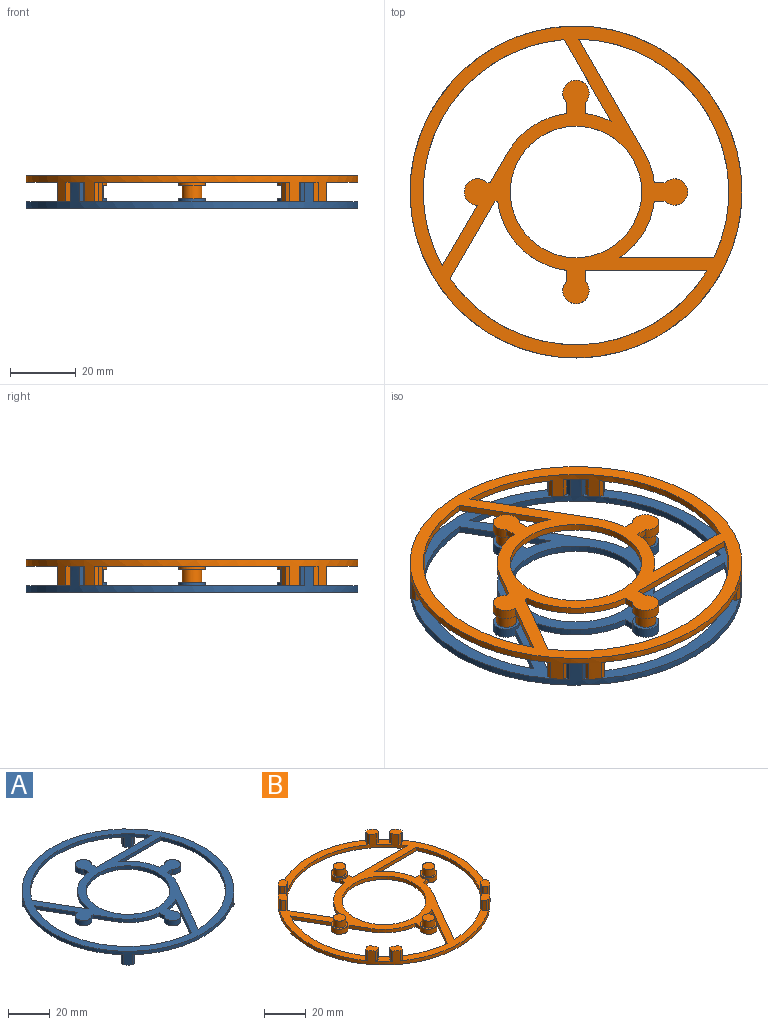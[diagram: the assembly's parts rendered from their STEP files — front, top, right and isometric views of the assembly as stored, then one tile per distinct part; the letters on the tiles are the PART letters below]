
ASSEMBLY  parts=2 mates=1
PART A: 64 faces, bbox 101x101x8 mm
  f0: plane 101x84.83mm, normal (0,0,-1), area 1819mm2, adj f2,f3,f4,f5,f6,f7,f8,f9
  f1: plane 68.66x16.42mm, normal (0,0,-1), area 284.2mm2, adj f3,f22,f37,f46,f48,f49,f50,f53
  f2: plane 23.61x13.63mm, normal (0.87,0.5,0), area 54.5mm2, adj f0,f3,f23,f27
  f3: cylinder r=46.5mm len=78.14mm, axis (0,0,1), area 227.1mm2, adj f0,f1,f2,f4,f27,f38,f47,f48
  f4: plane 37.08x2mm, normal (0,1,0), area 74.2mm2, adj f0,f3,f5,f27
  f5: plane 3.1x2mm, normal (1,0,0), area 6.2mm2, adj f0,f4,f27,f32
  f6: plane 3.25x2mm, normal (-1,0,0), area 6.5mm2, adj f0,f7,f27,f32
  f7: cylinder r=24mm len=21.09mm, axis (0,0,1), area 64.4mm2, adj f0,f6,f23,f27
  f8: cylinder r=46.5mm len=68.85mm, axis (0,0,1), area 206.4mm2, adj f0,f9,f24,f27,f41,f60,f62
  f9: plane 18.49x10.68mm, normal (-0.87,-0.5,0), area 42.7mm2, adj f0,f8,f27,f30
  f10: plane 2x0.97mm, normal (0,-1,0), area 1.9mm2, adj f0,f11,f27,f30
  f11: plane 9.25x5.34mm, normal (-0.87,-0.5,0), area 21.4mm2, adj f0,f10,f12,f27
  f12: cylinder r=24mm len=18.03mm, axis (0,0,1), area 44.8mm2, adj f0,f11,f13,f27
  f13: plane 3.25x2mm, normal (-1,0,0), area 6.5mm2, adj f0,f12,f27,f28
  f14: plane 3.25x2mm, normal (1,0,0), area 6.5mm2, adj f0,f15,f27,f28
  f15: cylinder r=24mm len=7.94mm, axis (0,0,1), area 16.6mm2, adj f0,f14,f24,f27
  f16: cylinder r=46.5mm len=66.49mm, axis (0,0,1), area 206.4mm2, adj f0,f17,f25,f27,f44,f58,f59
  f17: plane 34.49x19.91mm, normal (0.87,-0.5,0), area 79.7mm2, adj f0,f16,f18,f27
  f18: cylinder r=24mm len=9.25mm, axis (0,0,1), area 19.6mm2, adj f0,f17,f19,f27
  f19: plane 3.25x2mm, normal (0,-1,0), area 6.5mm2, adj f0,f18,f27,f34
  f20: plane 3.25x2mm, normal (0,1,0), area 6.5mm2, adj f0,f21,f27,f34
  f21: cylinder r=24mm len=17.25mm, axis (0,0,1), area 41.8mm2, adj f0,f20,f25,f27
  f22: cylinder r=50.5mm len=101mm, axis (0,0,1), area 726.7mm2, adj f0,f1,f27,f38,f41,f44,f47,f49
  f23: plane 2x0.84mm, normal (0,1,0), area 1.7mm2, adj f0,f2,f7,f27
  f24: plane 24.87x14.36mm, normal (-0.87,0.5,0), area 57.4mm2, adj f0,f8,f15,f27
  f25: plane 28.71x2mm, normal (0,-1,0), area 57.4mm2, adj f0,f16,f21,f27
  f26: cylinder r=20mm len=40mm, axis (0,0,1), area 251.3mm2, adj f0,f27
  f27: plane 101x101mm, normal (0,0,1), area 2386.5mm2, adj f2,f3,f4,f5,f6,f7,f8,f9
  f28: cylinder r=4mm len=8mm, axis (0,0,1), area 63.3mm2, adj f0,f13,f14,f27,f29
  f29: plane 8x8mm, normal (0,0,-1), area 50.3mm2, adj f28
  f30: cylinder r=4mm len=8mm, axis (0,0,1), area 56.7mm2, adj f0,f9,f10,f27,f31
  f31: plane 8x8mm, normal (0,0,-1), area 50.3mm2, adj f30
  f32: cylinder r=4mm len=8mm, axis (0,0,1), area 63.3mm2, adj f0,f5,f6,f27,f33
  f33: plane 8x8mm, normal (0,0,-1), area 50.3mm2, adj f32
  f34: cylinder r=4mm len=8mm, axis (0,0,1), area 63.3mm2, adj f0,f19,f20,f27,f35
  f35: plane 8x8mm, normal (0,0,-1), area 50.3mm2, adj f34
  f36: plane 6x1.49mm, normal (-0.66,-0.75,0), area 12mm2, adj f0,f38,f51,f52
  f37: plane 6x1.49mm, normal (0.75,0.66,0), area 12mm2, adj f1,f38,f50,f53
  f38: plane 5.47x5.47mm, normal (0,0,-1), area 20.6mm2, adj f3,f22,f36,f37,f50,f51,f52,f53
  f39: plane 6x1.49mm, normal (-0.66,0.75,0), area 12mm2, adj f0,f41,f60,f61
  f40: plane 6x1.49mm, normal (0.75,-0.66,0), area 12mm2, adj f0,f41,f62,f63
  f41: plane 5.47x5.47mm, normal (0,0,-1), area 20.6mm2, adj f8,f22,f39,f40,f60,f61,f62,f63
  f42: plane 6x1.49mm, normal (-0.75,-0.66,0), area 12mm2, adj f0,f44,f56,f58
  f43: plane 6x1.49mm, normal (0.66,0.75,0), area 12mm2, adj f0,f44,f57,f59
  f44: plane 5.47x5.47mm, normal (0,0,-1), area 20.6mm2, adj f16,f22,f42,f43,f56,f57,f58,f59
  f45: plane 6x1.49mm, normal (0.66,-0.75,0), area 12mm2, adj f0,f47,f54,f55
  f46: plane 6x1.49mm, normal (-0.75,0.66,0), area 12mm2, adj f1,f47,f48,f49
  f47: plane 5.47x5.47mm, normal (0,0,-1), area 20.6mm2, adj f3,f22,f45,f46,f48,f49,f54,f55
  f48: plane 6x1.4mm, normal (-1,-0.05,0), area 8.4mm2, adj f1,f3,f46,f47
  f49: plane 6x1.43mm, normal (-0.05,1,0), area 8.6mm2, adj f1,f22,f46,f47
  f50: plane 6x1.43mm, normal (0.05,1,0), area 8.6mm2, adj f1,f22,f37,f38
  f51: plane 6x1.43mm, normal (-1,-0.05,0), area 8.6mm2, adj f0,f22,f36,f38
  f52: plane 6x1.4mm, normal (0.05,-1,0), area 8.4mm2, adj f0,f3,f36,f38
  f53: plane 6x1.4mm, normal (1,-0.05,0), area 8.4mm2, adj f1,f3,f37,f38
  f54: plane 6x1.43mm, normal (1,-0.05,0), area 8.6mm2, adj f0,f22,f45,f47
  f55: plane 6x1.4mm, normal (-0.05,-1,0), area 8.4mm2, adj f0,f3,f45,f47
  f56: plane 6x1.43mm, normal (-0.05,-1,0), area 8.6mm2, adj f0,f22,f42,f44
  f57: plane 6x1.43mm, normal (1,0.05,0), area 8.6mm2, adj f0,f22,f43,f44
  f58: plane 6x1.4mm, normal (-1,0.05,0), area 8.4mm2, adj f0,f16,f42,f44
  f59: plane 6x1.4mm, normal (-0.05,1,0), area 8.4mm2, adj f0,f16,f43,f44
  f60: plane 6x1.4mm, normal (0.05,1,0), area 8.4mm2, adj f0,f8,f39,f41
  f61: plane 6x1.43mm, normal (-1,0.05,0), area 8.6mm2, adj f0,f22,f39,f41
  f62: plane 6x1.4mm, normal (1,0.05,0), area 8.4mm2, adj f0,f8,f40,f41
  f63: plane 6x1.43mm, normal (0.05,-1,0), area 8.6mm2, adj f0,f22,f40,f41
PART B: 104 faces, bbox 101x101x8 mm
  f0: plane 8.22x8.22mm, normal (0,0,1), area 24.6mm2, adj f7,f26,f67,f69,f75,f79,f80,f81
  f1: plane 101x80.3mm, normal (0,0,1), area 1683.5mm2, adj f6,f7,f8,f9,f10,f11,f12,f13
  f2: plane 8.22x8.22mm, normal (0,0,1), area 24.6mm2, adj f20,f26,f61,f63,f96,f97,f98,f99
  f3: plane 8.22x8.22mm, normal (0,0,1), area 24.6mm2, adj f12,f26,f55,f57,f100,f101,f102,f103
  f4: plane 59.59x12.98mm, normal (0,0,1), area 239mm2, adj f7,f26,f52,f70,f74,f76,f82,f84
  f5: plane 8.22x8.22mm, normal (0,0,1), area 24.6mm2, adj f7,f26,f49,f51,f72,f83,f85,f86
  f6: plane 23.61x13.63mm, normal (0.87,0.5,0), area 54.5mm2, adj f1,f7,f27,f31
  f7: cylinder r=46.5mm len=78.14mm, axis (0,0,-1), area 268.6mm2, adj f0,f1,f4,f5,f6,f8,f31,f50
  f8: plane 37.08x2mm, normal (0,1,0), area 74.2mm2, adj f1,f7,f9,f31
  f9: plane 3.1x2mm, normal (1,0,0), area 6.2mm2, adj f1,f8,f31,f36
  f10: plane 3.25x2mm, normal (-1,0,0), area 6.5mm2, adj f1,f11,f31,f36
  f11: cylinder r=24mm len=21.09mm, axis (0,0,-1), area 64.4mm2, adj f1,f10,f27,f31
  f12: cylinder r=46.5mm len=68.85mm, axis (0,0,-1), area 227.1mm2, adj f1,f3,f13,f28,f31,f56,f59,f92
  f13: plane 18.49x10.68mm, normal (-0.87,-0.5,0), area 42.7mm2, adj f1,f12,f31,f34
  f14: plane 2x0.97mm, normal (0,-1,0), area 1.9mm2, adj f1,f15,f31,f34
  f15: plane 9.25x5.34mm, normal (-0.87,-0.5,0), area 21.4mm2, adj f1,f14,f16,f31
  f16: cylinder r=24mm len=18.03mm, axis (0,0,-1), area 44.8mm2, adj f1,f15,f17,f31
  f17: plane 3.25x2mm, normal (-1,0,0), area 6.5mm2, adj f1,f16,f31,f32
  f18: plane 3.25x2mm, normal (1,0,0), area 6.5mm2, adj f1,f19,f31,f32
  f19: cylinder r=24mm len=7.94mm, axis (0,0,-1), area 16.6mm2, adj f1,f18,f28,f31
  f20: cylinder r=46.5mm len=66.49mm, axis (0,0,-1), area 227.1mm2, adj f1,f2,f21,f29,f31,f62,f65,f89
  f21: plane 34.49x19.91mm, normal (0.87,-0.5,0), area 79.7mm2, adj f1,f20,f22,f31
  f22: cylinder r=24mm len=9.25mm, axis (0,0,-1), area 19.6mm2, adj f1,f21,f23,f31
  f23: plane 3.25x2mm, normal (0,-1,0), area 6.5mm2, adj f1,f22,f31,f38
  f24: plane 3.25x2mm, normal (0,1,0), area 6.5mm2, adj f1,f25,f31,f38
  f25: cylinder r=24mm len=17.25mm, axis (0,0,-1), area 41.8mm2, adj f1,f24,f29,f31
  f26: cylinder r=50.5mm len=101mm, axis (0,0,-1), area 818.7mm2, adj f0,f1,f2,f3,f4,f5,f31,f50
  f27: plane 2x0.84mm, normal (0,1,0), area 1.7mm2, adj f1,f6,f11,f31
  f28: plane 24.87x14.36mm, normal (-0.87,0.5,0), area 57.4mm2, adj f1,f12,f19,f31
  f29: plane 28.71x2mm, normal (0,-1,0), area 57.4mm2, adj f1,f20,f25,f31
  f30: cylinder r=20mm len=40mm, axis (0,0,-1), area 251.3mm2, adj f1,f31
  f31: plane 101x101mm, normal (0,0,-1), area 2386.5mm2, adj f6,f7,f8,f9,f10,f11,f12,f13
  f32: cylinder r=4mm len=8mm, axis (0,0,-1), area 63.3mm2, adj f1,f17,f18,f31,f33
  f33: plane 8x8mm, normal (0,0,1), area 22mm2, adj f32,f44
  f34: cylinder r=4mm len=8mm, axis (0,0,-1), area 56.7mm2, adj f1,f13,f14,f31,f35
  f35: plane 8x8mm, normal (0,0,1), area 22mm2, adj f34,f42
  f36: cylinder r=4mm len=8mm, axis (0,0,-1), area 63.3mm2, adj f1,f9,f10,f31,f37
  f37: plane 8x8mm, normal (0,0,1), area 22mm2, adj f36,f40
  f38: cylinder r=4mm len=8mm, axis (0,0,-1), area 63.3mm2, adj f1,f23,f24,f31,f39
  f39: plane 8x8mm, normal (0,0,1), area 22mm2, adj f38,f46
  f40: cylinder r=3mm len=6mm, axis (0,0,-1), area 75.4mm2, adj f37,f41
  f41: plane 6x6mm, normal (0,0,1), area 28.3mm2, adj f40
  f42: cylinder r=3mm len=6mm, axis (0,0,-1), area 75.4mm2, adj f35,f43
  f43: plane 6x6mm, normal (0,0,1), area 28.3mm2, adj f42
  f44: cylinder r=3mm len=6mm, axis (0,0,-1), area 75.4mm2, adj f33,f45
  f45: plane 6x6mm, normal (0,0,1), area 28.3mm2, adj f44
  f46: cylinder r=3mm len=6mm, axis (0,0,-1), area 75.4mm2, adj f39,f47
  f47: plane 6x6mm, normal (0,0,1), area 28.3mm2, adj f46
  f48: plane 6x1.64mm, normal (-0.57,-0.82,0), area 12mm2, adj f1,f50,f73,f87
  f49: plane 6x1.49mm, normal (0.66,0.75,0), area 12mm2, adj f5,f50,f83,f86
  f50: plane 5.66x5.39mm, normal (0,0,1), area 20.6mm2, adj f7,f26,f48,f49,f73,f83,f86,f87
  f51: plane 6x1.49mm, normal (-0.75,-0.66,0), area 12mm2, adj f5,f53,f72,f85
  f52: plane 6x1.64mm, normal (0.82,0.57,0), area 12mm2, adj f4,f53,f82,f84
  f53: plane 5.66x5.39mm, normal (0,0,1), area 20.6mm2, adj f7,f26,f51,f52,f72,f82,f84,f85
  f54: plane 6x1.64mm, normal (-0.57,0.82,0), area 12mm2, adj f1,f56,f92,f93
  f55: plane 6x1.49mm, normal (0.66,-0.75,0), area 12mm2, adj f3,f56,f102,f103
  f56: plane 5.66x5.39mm, normal (0,0,1), area 20.6mm2, adj f12,f26,f54,f55,f92,f93,f102,f103
  f57: plane 6x1.49mm, normal (-0.75,0.66,0), area 12mm2, adj f3,f59,f100,f101
  f58: plane 6x1.64mm, normal (0.82,-0.57,0), area 12mm2, adj f1,f59,f94,f95
  f59: plane 5.66x5.39mm, normal (0,0,1), area 20.6mm2, adj f12,f26,f57,f58,f94,f95,f100,f101
  f60: plane 6x1.64mm, normal (-0.82,-0.57,0), area 12mm2, adj f1,f62,f90,f91
  f61: plane 6x1.49mm, normal (0.75,0.66,0), area 12mm2, adj f2,f62,f97,f99
  f62: plane 5.66x5.39mm, normal (0,0,1), area 20.6mm2, adj f20,f26,f60,f61,f90,f91,f97,f99
  f63: plane 6x1.49mm, normal (-0.66,-0.75,0), area 12mm2, adj f2,f65,f96,f98
  f64: plane 6x1.64mm, normal (0.57,0.82,0), area 12mm2, adj f1,f65,f88,f89
  f65: plane 5.66x5.39mm, normal (0,0,1), area 20.6mm2, adj f20,f26,f63,f64,f88,f89,f96,f98
  f66: plane 6x1.64mm, normal (0.57,-0.82,0), area 12mm2, adj f1,f68,f77,f78
  f67: plane 6x1.49mm, normal (-0.66,0.75,0), area 12mm2, adj f0,f68,f75,f79
  f68: plane 5.66x5.39mm, normal (0,0,1), area 20.6mm2, adj f7,f26,f66,f67,f75,f77,f78,f79
  f69: plane 6x1.49mm, normal (0.75,-0.66,0), area 12mm2, adj f0,f71,f80,f81
  f70: plane 6x1.64mm, normal (-0.82,0.57,0), area 12mm2, adj f4,f71,f74,f76
  f71: plane 5.66x5.39mm, normal (0,0,1), area 20.6mm2, adj f7,f26,f69,f70,f74,f76,f80,f81
  f72: plane 6x1.43mm, normal (-1,0.07,0), area 8.6mm2, adj f5,f26,f51,f53
  f73: plane 6x1.41mm, normal (-0.99,-0.16,0), area 8.6mm2, adj f1,f26,f48,f50
  f74: plane 6x1.38mm, normal (-0.99,-0.16,0), area 8.4mm2, adj f4,f7,f70,f71
  f75: plane 6x1.4mm, normal (-1,0.07,0), area 8.4mm2, adj f0,f7,f67,f68
  f76: plane 6x1.41mm, normal (-0.16,0.99,0), area 8.6mm2, adj f4,f26,f70,f71
  f77: plane 6x1.38mm, normal (-0.16,-0.99,0), area 8.4mm2, adj f1,f7,f66,f68
  f78: plane 6x1.41mm, normal (0.99,-0.16,0), area 8.6mm2, adj f1,f26,f66,f68
  f79: plane 6x1.43mm, normal (0.07,1,0), area 8.6mm2, adj f0,f26,f67,f68
  f80: plane 6x1.4mm, normal (0.07,-1,0), area 8.4mm2, adj f0,f7,f69,f71
  f81: plane 6x1.43mm, normal (1,0.07,0), area 8.6mm2, adj f0,f26,f69,f71
  f82: plane 6x1.41mm, normal (0.16,0.99,0), area 8.6mm2, adj f4,f26,f52,f53
  f83: plane 6x1.43mm, normal (-0.07,1,0), area 8.6mm2, adj f5,f26,f49,f50
  f84: plane 6x1.38mm, normal (0.99,-0.16,0), area 8.4mm2, adj f4,f7,f52,f53
  f85: plane 6x1.4mm, normal (-0.07,-1,0), area 8.4mm2, adj f5,f7,f51,f53
  f86: plane 6x1.4mm, normal (1,0.07,0), area 8.4mm2, adj f5,f7,f49,f50
  f87: plane 6x1.38mm, normal (0.16,-0.99,0), area 8.4mm2, adj f1,f7,f48,f50
  f88: plane 6x1.41mm, normal (0.99,0.16,0), area 8.6mm2, adj f1,f26,f64,f65
  f89: plane 6x1.38mm, normal (-0.16,0.99,0), area 8.4mm2, adj f1,f20,f64,f65
  f90: plane 6x1.41mm, normal (-0.16,-0.99,0), area 8.6mm2, adj f1,f26,f60,f62
  f91: plane 6x1.38mm, normal (-0.99,0.16,0), area 8.4mm2, adj f1,f20,f60,f62
  f92: plane 6x1.38mm, normal (0.16,0.99,0), area 8.4mm2, adj f1,f12,f54,f56
  f93: plane 6x1.41mm, normal (-0.99,0.16,0), area 8.6mm2, adj f1,f26,f54,f56
  f94: plane 6x1.38mm, normal (0.99,0.16,0), area 8.4mm2, adj f1,f12,f58,f59
  f95: plane 6x1.41mm, normal (0.16,-0.99,0), area 8.6mm2, adj f1,f26,f58,f59
  f96: plane 6x1.4mm, normal (-1,-0.07,0), area 8.4mm2, adj f2,f20,f63,f65
  f97: plane 6x1.43mm, normal (1,-0.07,0), area 8.6mm2, adj f2,f26,f61,f62
  f98: plane 6x1.43mm, normal (0.07,-1,0), area 8.6mm2, adj f2,f26,f63,f65
  f99: plane 6x1.4mm, normal (0.07,1,0), area 8.4mm2, adj f2,f20,f61,f62
  f100: plane 6x1.4mm, normal (-0.07,1,0), area 8.4mm2, adj f3,f12,f57,f59
  f101: plane 6x1.43mm, normal (-1,-0.07,0), area 8.6mm2, adj f3,f26,f57,f59
  f102: plane 6x1.4mm, normal (1,-0.07,0), area 8.4mm2, adj f3,f12,f55,f56
  f103: plane 6x1.43mm, normal (-0.07,-1,0), area 8.6mm2, adj f3,f26,f55,f56
PLACE A rot(axis=(1,0,0),180deg) t=(1.09,0.52,5.84)mm
PLACE B rot(axis=(1,0,0),180deg) t=(1.09,0.52,15.84)mm
MATE fastened B.f30 <-> A.f26  axis (0,0,1) through (1.09,0.52,15.84)mm
